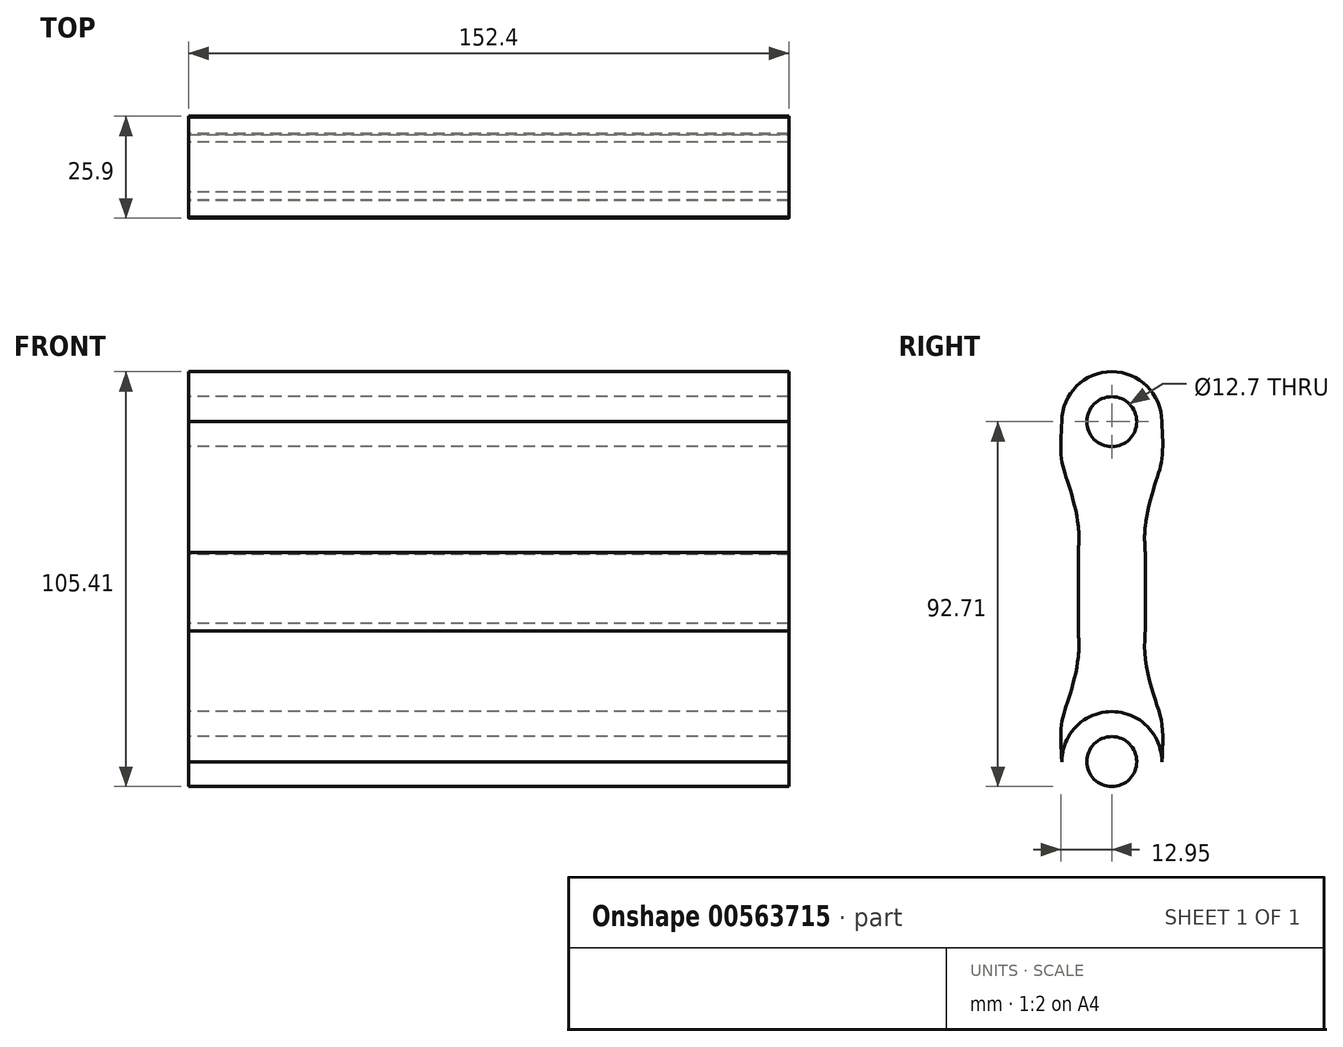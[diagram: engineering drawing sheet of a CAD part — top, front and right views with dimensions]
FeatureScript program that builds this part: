
annotation { "Feature Type Name" : "Feature", "Feature Type Description" : "" }
export const myFeature = defineFeature(function(context is Context, id is Id, definition is map)
    precondition{}
    {
        {
            var Q0;
            Q0=qCreatedBy(makeId("Right.planeOp"),FACE);
            var sketch = newSketch(context, id + "F0", { "sketchPlane" : qUnion([Q0])});
            skCircle(sketch, "E0", {"center": v(0, 43.18) * mm, "radius": 12.7 * mm});
            skCircle(sketch, "E1", {"center": v(0, 43.18) * mm, "radius": 6.35 * mm});
            skFitSpline(sketch, "E2", {"points": [v(12.7, 43.26) * mm, v(12.79, 33.97) * mm, v(11.15, 27.84) * mm, v(8.5, 16.6) * mm, v(8.6, 8.08) * mm, v(9, 0) * mm], "startDerivative": vector(2.89, -47.99) * mm, "endDerivative": vector(6.35, -42.96) * mm});
            skCircle(sketch, "E3.MirrorC", {"center": v(0, -43.18) * mm, "radius": 6.35 * mm});
            skCircle(sketch, "E4.MirrorC", {"center": v(0, -43.18) * mm, "radius": 12.7 * mm});
            skFitSpline(sketch, "E5.MirrorCS", {"points": [v(12.7, -43.26) * mm, v(12.79, -33.97) * mm, v(11.15, -27.84) * mm, v(8.5, -16.6) * mm, v(8.6, -8.08) * mm, v(9, 0) * mm], "startDerivative": vector(2.89, 47.99) * mm, "endDerivative": vector(6.35, 42.96) * mm});
            skFitSpline(sketch, "E6.MirrorCS", {"points": [v(-12.7, 43.26) * mm, v(-12.79, 33.97) * mm, v(-11.15, 27.84) * mm, v(-8.5, 16.6) * mm, v(-8.6, 8.08) * mm, v(-9, 0) * mm], "startDerivative": vector(-2.89, -47.99) * mm, "endDerivative": vector(-6.35, -42.96) * mm});
            skFitSpline(sketch, "E7.MirrorCS", {"points": [v(-12.7, -43.26) * mm, v(-12.79, -33.97) * mm, v(-11.15, -27.84) * mm, v(-8.5, -16.6) * mm, v(-8.6, -8.08) * mm, v(-9, 0) * mm], "startDerivative": vector(-2.89, 47.99) * mm, "endDerivative": vector(-6.35, 42.96) * mm});
            skLineSegment(sketch, "E8", {"start": v(-8.5, 16.6) * mm, "end": v(-8.5, -16.6) * mm});
            skLineSegment(sketch, "E9", {"start": v(8.5, 16.6) * mm, "end": v(8.6, -8.08) * mm});
            skSolve(sketch);
        }
        {
            var Q0;
            Q0=makeQuery(id+"F0.imprint","IMPRINT",FACE,{"disambiguationData":[TD([[makeQuery(id+"F0.imprint","IMPRINT",EDGE,{"derivedFrom":sQuery(id+"F0.wireOp",EDGE,"E1")}),-1.0]])]});
            var Q1;
            {var subQ3=sQuery(id+"F0.wireOp",EDGE,"E2");Q1=makeQuery(id+"F0.imprint","IMPRINT",FACE,{"disambiguationData":[TD([[makeQuery(id+"F0.imprint","IMPRINT",EDGE,{"derivedFrom":subQ3}),-1.0]])]});}
            var Q2;
            Q2=makeQuery(id+"F0.imprint","IMPRINT",FACE,{"disambiguationData":[TD([[makeQuery(id+"F0.imprint","IMPRINT",EDGE,{"derivedFrom":sQuery(id+"F0.wireOp",EDGE,"E3.MirrorC")}),1.0]])]});
            extrude(context, id + "F1", {"entities" : qUnion([Q0, Q1, Q2]), "endBound" : BoundingType.SYMMETRIC, "depth" : 152.4 * mm});
        }
    });
